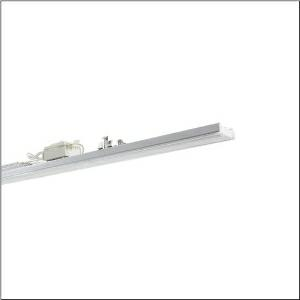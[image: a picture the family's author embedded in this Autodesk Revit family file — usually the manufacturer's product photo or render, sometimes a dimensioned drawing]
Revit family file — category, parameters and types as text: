
# Revit family: licross_r__21_recessed_mo_52tl11dn455g_e53e
name_source: partatom
category: Lighting Fixtures
units: mm (PartAtom-declared; Revit-internal decimal feet)

## family parameters
Cut with Voids When Loaded = No
Host = Face
Light Source = No
Part Type = Normal
Room Calculation Point = No
Round Connector Dimension = Use Diameter
Shared = No

## types (1)
- --- (1 x LED, 5800 lm, 31.8 W, 4000K)
    Apparent Load = 32 VA
    CIE Flux Codes = 89 96 99 100 100
    Color Rendering = 80
    Color Temperature = 4000K
    Default Elevation = 1800 mm
    Description = Licross® 21 Recessed MO, luminaire insert, of sheet steel, galvanised, coil coated, white, length: 1.500mm, width: 66mm, height: 67mm, LED rated luminous flux: 5.800lm, light colour: 840, control gear: DALI 2, with plug, 5-pole, with phase selection, mains connection: 220..240V, AC, 50/60Hz, rated input power: 32W, halogen-free wiring, primary light control with lens, of plastic, primary optical cover: cover, of PMMA, light emission: direct distribution, primary light characteristic: symmetric, protection rating (complete): IP40, insulation class (complete): insulation class I (protective earthing), certification: CE, ENEC, VDE, UKCA, protection symbol: D if used in an environment without relevant dust loads with corresponding accessories, impact resistance: IK06, permissible ambient temperature for indoor applications: -25..+45°C, corresponds to IFS (International Featured Standards) requirements for safety and quality in the food industry, reducing of maximum allowable ambient temperature of 5°C with ceiling mounting, LABS conformity tested according to VDMA 24364:2018-05, packaging unit: 1 piece
    Height = 58 mm
    Lamp = 1 x LED
    Lamp Light Flux = 5800 lm
    Lamp Power = 31.8 W
    Lamp count = 1
    Length = 1500 mm
    Luminous efficacy = 182 lm/W
    Manufacturer = Siteco
    ModVariant = No
    Model = 52TL11DN455G
    Mounting Place = Ceiling
    Mounting Type = Pendant
    Number of Poles = 1
    OnlyDefault = Yes
    Power Factor = 1
    Product Name = Licross® 21 Recessed MO
    Product group = luminaire insert
    ProductGroupID = 902
    Protection Class = Protection class I
    Protection Degree = IP 40
    RLX_Detail_Level = 1
    RLX_Emergency_Light_Flux = 0 lm
    RLX_Emergency_Type = 0
    RLX_Emergency_Type_DB = No
    RlxData = <blob elided: 24153 chars, md5=5cd742f8>
    Socket = socket
    Standby Power = 0 W
    System Light Flux = 5800 lm
    System Power = 32 W
    Type Comments = factory setting: luminous flux: 100 % | dim-lin: 254 | 215 mA
    Type Image = l_1296930.jpg
    URL = http://relux.com
    VarID = @adj_126890
    Voltage = 0 V
    Weight = 0.00 kg
    Width = 66 mm

## geometry (parser evidence)
native form markers: Blend x4, Sweep x9
no freeform markers — native parametric forms only
